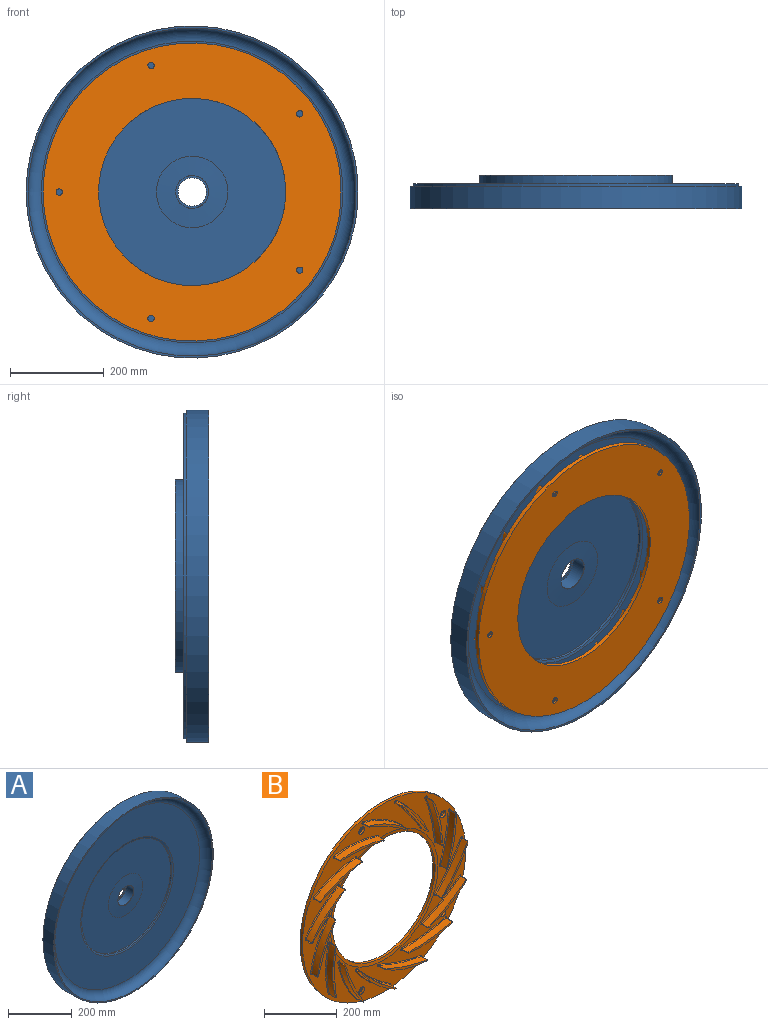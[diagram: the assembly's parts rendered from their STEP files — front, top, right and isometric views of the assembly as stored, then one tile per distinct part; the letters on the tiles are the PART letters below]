
ASSEMBLY  parts=2 mates=1
PART A: 22 faces, bbox 756.3x71.4x756.3 mm
  f0: plane 70.31x70.31mm, normal (0,-1,0), area 2.8mm2, adj f13,f19
  f1: cylinder r=353.69mm len=707.39mm, axis (0,1,0), area 105918.4mm2, adj f2,f18
  f2: plane 707.39x707.39mm, normal (0,1,0), area 15922.8mm2, adj f1,f3
  f3: cylinder r=346.46mm len=692.91mm, axis (0,1,0), area 11887.8mm2, adj f2,f4
  f4: plane 692.91x692.91mm, normal (0,1,0), area 45663.4mm2, adj f3,f5
  f5: cylinder r=324.8mm len=649.61mm, axis (0,1,0), area 1658.8mm2, adj f4,f6
  f6: plane 649.61x649.61mm, normal (0,1,0), area 165425.1mm2, adj f5,f7
  f7: cylinder r=229.87mm len=459.74mm, axis (0,1,0), area 2237.8mm2, adj f6,f8
  f8: plane 459.74x459.74mm, normal (0,1,0), area 33186.2mm2, adj f7,f9
  f9: cylinder r=205.61mm len=411.23mm, axis (0,1,0), area 22674.7mm2, adj f8,f10
  f10: plane 411.23x411.23mm, normal (0,1,0), area 129967.7mm2, adj f9,f11
  f11: cylinder r=30.11mm len=60.22mm, axis (0,1,0), area 673.4mm2, adj f10,f12
  f12: plane 70.28x70.28mm, normal (0,-1,0), area 1031mm2, adj f11,f13
  f13: cylinder r=35.14mm len=70.28mm, axis (0,1,0), area 7213.9mm2, adj f0,f12
  f14: plane 398.78x398.78mm, normal (0,-1,0), area 106656.9mm2, adj f20,f21
  f15: cone r=205.61mm half-angle=75deg, axis (0,-1,0), area 8197.2mm2, adj f16,f21
  f16: plane 642.6x642.6mm, normal (0,-1,0), area 191501.9mm2, adj f15,f17
  f17: torus R=321.3mm, axis (0,1,0), area 93988.3mm2, adj f16,f18
  f18: plane 707.39x707.39mm, normal (0,-1,0), area 9537.5mm2, adj f1,f17
  f19: cylinder r=35.15mm len=70.31mm, axis (0,1,0), area 280.5mm2, adj f0,f20
  f20: cone r=76.2mm half-angle=88.2deg, axis (0,1,0), area 14366mm2, adj f14,f19
  f21: cylinder r=199.39mm len=398.78mm, axis (0,1,0), area 6808.4mm2, adj f14,f15
PART B: 60 faces, bbox 635.3x40.2x635.3 mm
  f0: bspline ~170.28x37.7mm, area 8052.8mm2, adj f1,f6
  f1: plane 170.57x38.02mm, normal (0,-1,0), area 1189mm2, adj f0
  f2: cylinder r=199.39mm len=398.78mm, axis (0,1,0), area 10501mm2, adj f3,f59
  f3: plane 635x635mm, normal (0,1,0), area 191079mm2, adj f2,f4,f49,f51,f53,f55,f57
  f4: cylinder r=317.5mm len=635mm, axis (0,1,0), area 18748.2mm2, adj f3,f5
  f5: plane 635x635mm, normal (0,-1,0), area 148873.6mm2, adj f4,f6,f9,f12,f15,f18,f21,f24
  f6: bspline ~175.32x42.77mm, area 1426.7mm2, adj f0,f5
  f7: plane 170.07x39.85mm, normal (0,-1,0), area 1189mm2, adj f8
  f8: bspline ~168.18x39.5mm, area 8052.8mm2, adj f7,f9
  f9: bspline ~174.82x44.62mm, area 1426.7mm2, adj f5,f8
  f10: plane 140.44x104.04mm, normal (0,-1,0), area 1189mm2, adj f11
  f11: bspline ~140.21x103.82mm, area 8052.8mm2, adj f10,f12
  f12: bspline ~145.19x108.79mm, area 1426.7mm2, adj f5,f11
  f13: plane 151.57x87.02mm, normal (0,-1,0), area 1189mm2, adj f14
  f14: bspline ~151.43x86.73mm, area 8052.8mm2, adj f13,f15
  f15: bspline ~156.32x91.76mm, area 1426.7mm2, adj f5,f14
  f16: plane 173.27x24.02mm, normal (0,-1,0), area 1189mm2, adj f17
  f17: bspline ~171.42x23.61mm, area 8052.8mm2, adj f16,f18
  f18: bspline ~178.02x28.77mm, area 1426.7mm2, adj f5,f17
  f19: plane 165.28x56.62mm, normal (0,-1,0), area 1189mm2, adj f20
  f20: bspline ~164.98x56.3mm, area 8052.8mm2, adj f19,f21
  f21: bspline ~170.02x61.37mm, area 1426.7mm2, adj f5,f20
  f22: plane 129x117.94mm, normal (0,-1,0), area 1189mm2, adj f23
  f23: bspline ~128.7x117.63mm, area 8052.8mm2, adj f22,f24
  f24: bspline ~133.74x122.69mm, area 1426.7mm2, adj f5,f23
  f25: plane 159.66x71.05mm, normal (0,-1,0), area 1189mm2, adj f26
  f26: bspline ~159.53x70.75mm, area 8052.8mm2, adj f25,f27
  f27: bspline ~164.4x75.79mm, area 1426.7mm2, adj f5,f26
  f28: plane 174.09x14.55mm, normal (0,-1,0), area 1189mm2, adj f29
  f29: bspline ~173.94x30.48mm, area 8052.8mm2, adj f28,f30
  f30: bspline ~178.84x19.29mm, area 1426.7mm2, adj f5,f29
  f31: plane 158.68x73.18mm, normal (0,-1,0), area 1189mm2, adj f32
  f32: bspline ~158.49x72.92mm, area 8052.8mm2, adj f31,f33
  f33: bspline ~163.43x77.93mm, area 1426.7mm2, adj f5,f32
  f34: plane 130.6x116.17mm, normal (0,-1,0), area 1189mm2, adj f35
  f35: bspline ~128.88x114.26mm, area 8052.8mm2, adj f34,f36
  f36: bspline ~135.34x120.92mm, area 1426.7mm2, adj f5,f35
  f37: plane 166.02x54.42mm, normal (0,-1,0), area 1189mm2, adj f38
  f38: bspline ~165.89x54.11mm, area 8052.8mm2, adj f37,f39
  f39: bspline ~170.76x59.16mm, area 1426.7mm2, adj f5,f38
  f40: plane 173.02x25.44mm, normal (0,-1,0), area 1189mm2, adj f41
  f41: bspline ~171.14x25.07mm, area 8052.8mm2, adj f40,f42
  f42: bspline ~177.77x30.17mm, area 1426.7mm2, adj f5,f41
  f43: plane 150.38x89.06mm, normal (0,-1,0), area 1189mm2, adj f44
  f44: bspline ~150.17x88.81mm, area 8052.8mm2, adj f43,f45
  f45: bspline ~155.12x93.8mm, area 1426.7mm2, adj f5,f44
  f46: plane 141.85x102.12mm, normal (0,-1,0), area 1189mm2, adj f47
  f47: bspline ~140.11x100.69mm, area 8052.8mm2, adj f46,f48
  f48: bspline ~146.6x106.86mm, area 1426.7mm2, adj f5,f47
  f49: cylinder r=6.75mm len=13.49mm, axis (0,-1,0), area 185.5mm2, adj f3,f50
  f50: cone r=11.11mm half-angle=41deg, axis (0,-1,0), area 373.4mm2, adj f5,f49
  f51: cylinder r=6.75mm len=13.49mm, axis (0,-1,0), area 185.5mm2, adj f3,f52
  f52: cone r=11.11mm half-angle=41deg, axis (0,-1,0), area 373.4mm2, adj f5,f51
  f53: cylinder r=6.75mm len=13.49mm, axis (0,-1,0), area 185.5mm2, adj f3,f54
  f54: cone r=11.11mm half-angle=41deg, axis (0,-1,0), area 373.4mm2, adj f5,f53
  f55: cylinder r=6.75mm len=13.49mm, axis (0,-1,0), area 185.5mm2, adj f3,f56
  f56: cone r=11.11mm half-angle=41deg, axis (0,-1,0), area 373.4mm2, adj f5,f55
  f57: cylinder r=6.75mm len=13.49mm, axis (0,-1,0), area 185.5mm2, adj f3,f58
  f58: cone r=11.11mm half-angle=41deg, axis (0,-1,0), area 373.4mm2, adj f5,f57
  f59: cone r=209.55mm half-angle=84.3deg, axis (0,-1,0), area 13117.9mm2, adj f2,f5
PLACE A t=(-163.61,45.14,-25.65)mm fixed
PLACE B rot(axis=(1,0,0),180deg) t=(-163.61,79.94,-25.65)mm
MATE fastened B.f2 <-> A.f1  axis (0,-1,0) through (-163.61,45.14,-25.65)mm
